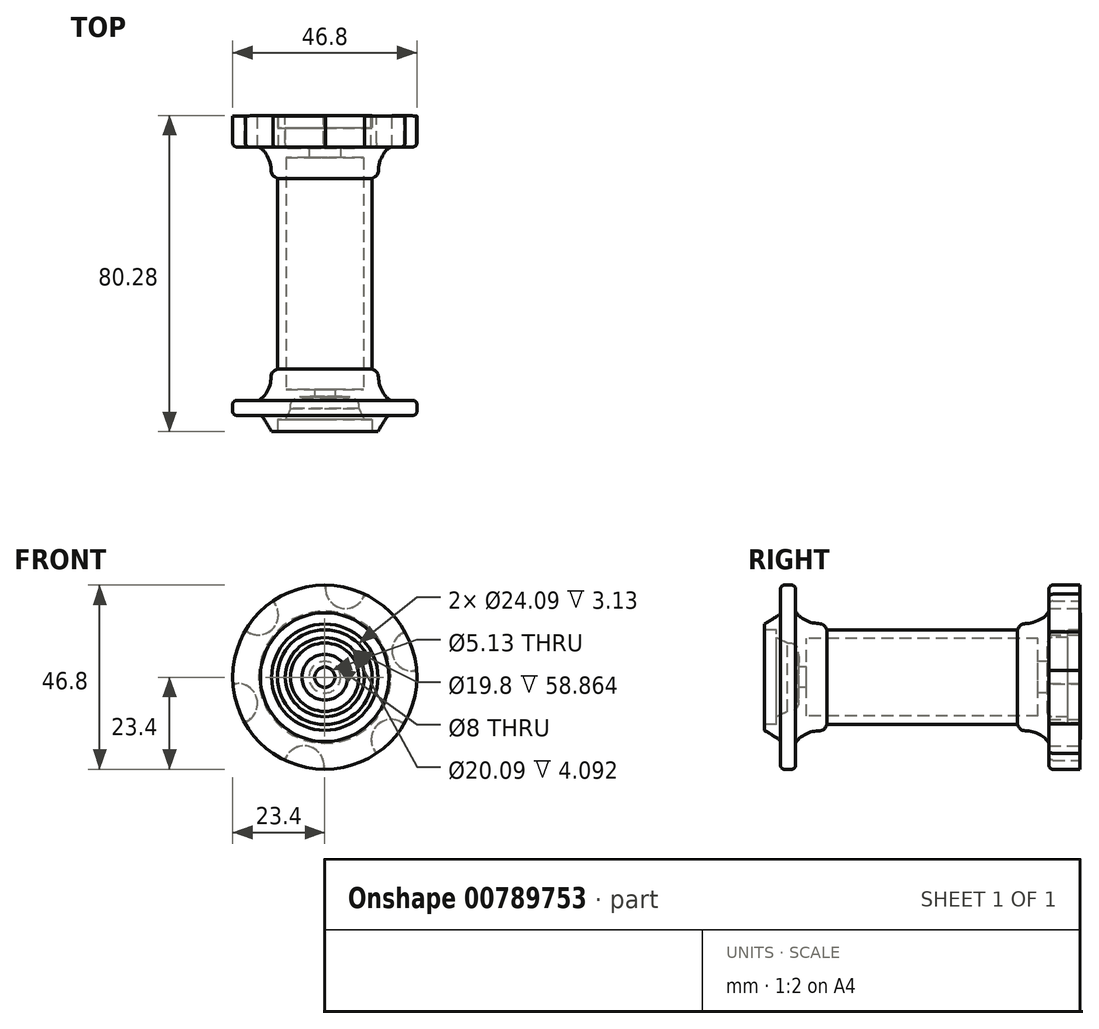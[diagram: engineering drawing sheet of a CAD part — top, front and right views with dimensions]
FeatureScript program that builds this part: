
annotation { "Feature Type Name" : "Feature", "Feature Type Description" : "" }
export const myFeature = defineFeature(function(context is Context, id is Id, definition is map)
    precondition{}
    {
        {
            var Q0;
            Q0=qCreatedBy(makeId("Top.planeOp"),FACE);
            var sketch = newSketch(context, id + "F0", { "sketchPlane" : qUnion([Q0])});
            skLineSegment(sketch, "E0", {"start": v(0, 0) * mm, "end": v(0, 40.14) * mm});
            skLineSegment(sketch, "E1", {"start": v(-12.04, 0) * mm, "end": v(-12.04, 24.2) * mm});
            skPoint(sketch, "E2", {"position": v(-12.04, 24.2) * mm});
            skPoint(sketch, "E3", {"position": v(-12.04, 32.2) * mm});
            skFitSpline(sketch, "E4", {"points": [v(-12.04, 24.2) * mm, v(-13.4, 25.25) * mm, v(-13.82, 27.81) * mm, v(-15.53, 31.24) * mm, v(-16.8, 32.2) * mm], "startDerivative": vector(-7.76, 4.32) * mm, "endDerivative": vector(-4.98, 2.58) * mm});
            skLineSegment(sketch, "E5", {"start": v(-16.8, 32.2) * mm, "end": v(-23.4, 32.2) * mm});
            skPoint(sketch, "E6", {"position": v(0, 31.31) * mm});
            skPoint(sketch, "E7", {"position": v(0, 37) * mm});
            skPoint(sketch, "E8.orphan", {"position": v(0, 36) * mm});
            skPoint(sketch, "E9.orphan", {"position": v(0, 32.2) * mm});
            skLineSegment(sketch, "E10", {"start": v(-12.04, 37) * mm, "end": v(-10.04, 37) * mm});
            skLineSegment(sketch, "E11", {"start": v(-4, 29.43) * mm, "end": v(-9.9, 29.43) * mm});
            skLineSegment(sketch, "E12", {"start": v(-9.9, 29.43) * mm, "end": v(-9.9, 0) * mm});
            skPoint(sketch, "E13.orphan", {"position": v(-2.05, 0) * mm});
            skLineSegment(sketch, "E14.trimOffspring", {"start": v(-12.04, 37) * mm, "end": v(-12.04, 40.14) * mm});
            skPoint(sketch, "E15.orphan", {"position": v(-12.04, 36) * mm});
            skLineSegment(sketch, "E16.MirrorCS", {"start": v(-12.04, -40.14) * mm, "end": v(-13.5, -40.14) * mm});
            skFitSpline(sketch, "E17.MirrorCS", {"points": [v(-16.34, -36) * mm, v(-15.1, -37.47) * mm, v(-14.32, -38.72) * mm, v(-13.5, -40.14) * mm], "startDerivative": vector(2.26, 0.32) * mm, "endDerivative": vector(2.5, -4.5) * mm});
            skLineSegment(sketch, "E18.MirrorCS", {"start": v(-23.4, -36) * mm, "end": v(-16.34, -36) * mm});
            skLineSegment(sketch, "E19.MirrorCS", {"start": v(-23.4, -32.2) * mm, "end": v(-23.4, -36) * mm});
            skLineSegment(sketch, "E20.MirrorCS", {"start": v(-16.8, -32.2) * mm, "end": v(-23.4, -32.2) * mm});
            skPoint(sketch, "E21.MirrorP", {"position": v(-12.04, -32.2) * mm});
            skLineSegment(sketch, "E22.MirrorCS", {"start": v(-2.57, -29.43) * mm, "end": v(-9.9, -29.43) * mm});
            skLineSegment(sketch, "E23.MirrorCS", {"start": v(-2.57, -31.31) * mm, "end": v(-2.57, -29.43) * mm});
            skFitSpline(sketch, "E24.MirrorCS", {"points": [v(-10.04, -37) * mm, v(-2.57, -31.31) * mm], "startDerivative": vector(6.81, 11.06) * mm, "endDerivative": vector(18.63, -1.06) * mm});
            skLineSegment(sketch, "E25.MirrorCS", {"start": v(-12.04, -37) * mm, "end": v(-12.04, -40.14) * mm});
            skLineSegment(sketch, "E26.MirrorCS", {"start": v(-12.04, -37) * mm, "end": v(-10.04, -37) * mm});
            skPoint(sketch, "E27.MirrorP", {"position": v(-12.04, -36) * mm});
            skFitSpline(sketch, "E28.MirrorCS", {"points": [v(-12.04, -24.2) * mm, v(-13.4, -25.25) * mm, v(-13.82, -27.81) * mm, v(-15.53, -31.24) * mm, v(-16.8, -32.2) * mm], "startDerivative": vector(-7.76, -4.32) * mm, "endDerivative": vector(-4.98, -2.58) * mm});
            skLineSegment(sketch, "E29", {"start": v(-12.04, 0) * mm, "end": v(-12.04, -24.2) * mm});
            skLineSegment(sketch, "E30", {"start": v(-9.9, -29.43) * mm, "end": v(-9.9, 0) * mm});
            skLineSegment(sketch, "E31", {"start": v(-4, 29.43) * mm, "end": v(-4, 31.86) * mm});
            skPoint(sketch, "E32.end.orphan", {"position": v(-0.6, 29.43) * mm});
            skPoint(sketch, "E32.start.orphan", {"position": v(0, 29.43) * mm});
            skCircle(sketch, "E33", {"center": v(-6.36, -33.78) * mm, "radius": 2.38 * mm});
            skPoint(sketch, "E34", {"position": v(-7.66, -32.5) * mm});
            skLineSegment(sketch, "E35", {"start": v(-10.04, 37) * mm, "end": v(-10.04, 32.92) * mm});
            skLineSegment(sketch, "E36", {"start": v(-8.99, 31.86) * mm, "end": v(-4, 31.86) * mm});
            skPoint(sketch, "E37.visualSharp", {"position": v(-10.04, 31.86) * mm});
            skArc(sketch, "E37.filletArc", {"start": v(-10.04, 32.92) * mm, "mid": v(-9.73, 32.17) * mm, "end": v(-8.99, 31.86) * mm});
            skLineSegment(sketch, "E38", {"start": v(-23.4, 32.2) * mm, "end": v(-23.4, 40.08) * mm});
            skLineSegment(sketch, "E39", {"start": v(-23.4, 40.08) * mm, "end": v(-12.04, 40.14) * mm});
            skSolve(sketch);
        }
        {
            var Q0;
            Q0=makeQuery(id+"F0.imprint","IMPRINT",FACE,{"disambiguationData":[TD([[makeQuery(id+"F0.imprint","IMPRINT",EDGE,{"derivedFrom":sQuery(id+"F0.wireOp",EDGE,"E1")}),-1.0]])]});
            var Q1;
            Q1=sQuery(id+"F0.wireOp",EDGE,"E0");
            revolve(context, id + "F1", {"surfaceOperationType" : NewSurfaceOperationType.NEW, "entities" : qUnion([Q0]), "axis" : qUnion([Q1]), "revolveType" : RevolveType.FULL});
        }
        {
            var Q0;
            Q0=makeQuery(id+"F1.opRevolve","SWEPT_EDGE",EDGE,{"disambiguationData":[OSD([sQuery(id+"F0.wireOp",EDGE,"vuaXWecF-eVP0-qpJy-XoME-ukMJib7b6FMQ"),sQuery(id+"F0.wireOp",EDGE,"89ZEt2hK-1O52-Bouf-ums8-g1A8w5U9HYQ6")])]});
            var Q1;
            Q1=makeQuery(id+"F1.opRevolve","SWEPT_EDGE",EDGE,{"disambiguationData":[OSD([sQuery(id+"F0.wireOp",EDGE,"E5"),sQuery(id+"F0.wireOp",EDGE,"vuaXWecF-eVP0-qpJy-XoME-ukMJib7b6FMQ")])]});
            var Q2;
            Q2=makeQuery(id+"F1.opRevolve","SWEPT_EDGE",EDGE,{"disambiguationData":[OSD([sQuery(id+"F0.wireOp",EDGE,"E19.MirrorCS"),sQuery(id+"F0.wireOp",EDGE,"E20.MirrorCS")])]});
            var Q3;
            Q3=makeQuery(id+"F1.opRevolve","SWEPT_EDGE",EDGE,{"disambiguationData":[OSD([sQuery(id+"F0.wireOp",EDGE,"E18.MirrorCS"),sQuery(id+"F0.wireOp",EDGE,"E19.MirrorCS")])]});
            fillet(context, id + "F2", {"entities" : qUnion([Q0, Q1, Q2, Q3]), "radius" : 1 * mm, "tangentPropagation" : true, "allowEdgeOverflow" : false});
        }
        {
            var Q0;
            Q0=sQuery(id+"F0.wireOp",VERTEX,"E39.start");
            var Q1;
            Q1=qCreatedBy(makeId("Front.planeOp"),FACE);
            cPlane(context, id + "F3", {"entities" : qUnion([Q0, Q1]), "cplaneType" : CPlaneType.PLANE_POINT, "offset" : 25 * mm, "width" : 150 * mm, "height" : 150 * mm});
        }
        {
            var Q0;
            Q0=qCreatedBy(id+"F3.planeOp",FACE);
            var sketch = newSketch(context, id + "F4", { "sketchPlane" : qUnion([Q0])});
            skCircle(sketch, "E40", {"center": v(-5.27, -22.55) * mm, "radius": 5.09 * mm});
            skCircle(sketch, "E41.1.0", {"center": v(16.9, -15.84) * mm, "radius": 5.09 * mm});
            skCircle(sketch, "E41.2.0", {"center": v(22.16, 6.71) * mm, "radius": 5.09 * mm});
            skPoint(sketch, "E41.center", {"position": v(0, 0) * mm});
            skCircle(sketch, "E42.1.3.0", {"center": v(5.27, 22.55) * mm, "radius": 5.09 * mm});
            skCircle(sketch, "E42.1.4.0", {"center": v(-16.9, 15.84) * mm, "radius": 5.09 * mm});
            skCircle(sketch, "E42.1.5.0", {"center": v(-22.16, -6.71) * mm, "radius": 5.09 * mm});
            skSolve(sketch);
        }
        {
            var Q0;
            Q0 = qSketchRegion(id + "F4", true);
            extrude(context, id + "F5", {"entities" : qUnion([Q0]), "operationType" : NewBodyOperationType.REMOVE, "depth" : 25 * mm, "offsetDistance" : 25 * mm, "hasSecondDirection" : true, "secondDirectionOppositeDirection" : true, "secondDirectionDepth" : 25 * mm});
        }
    });
